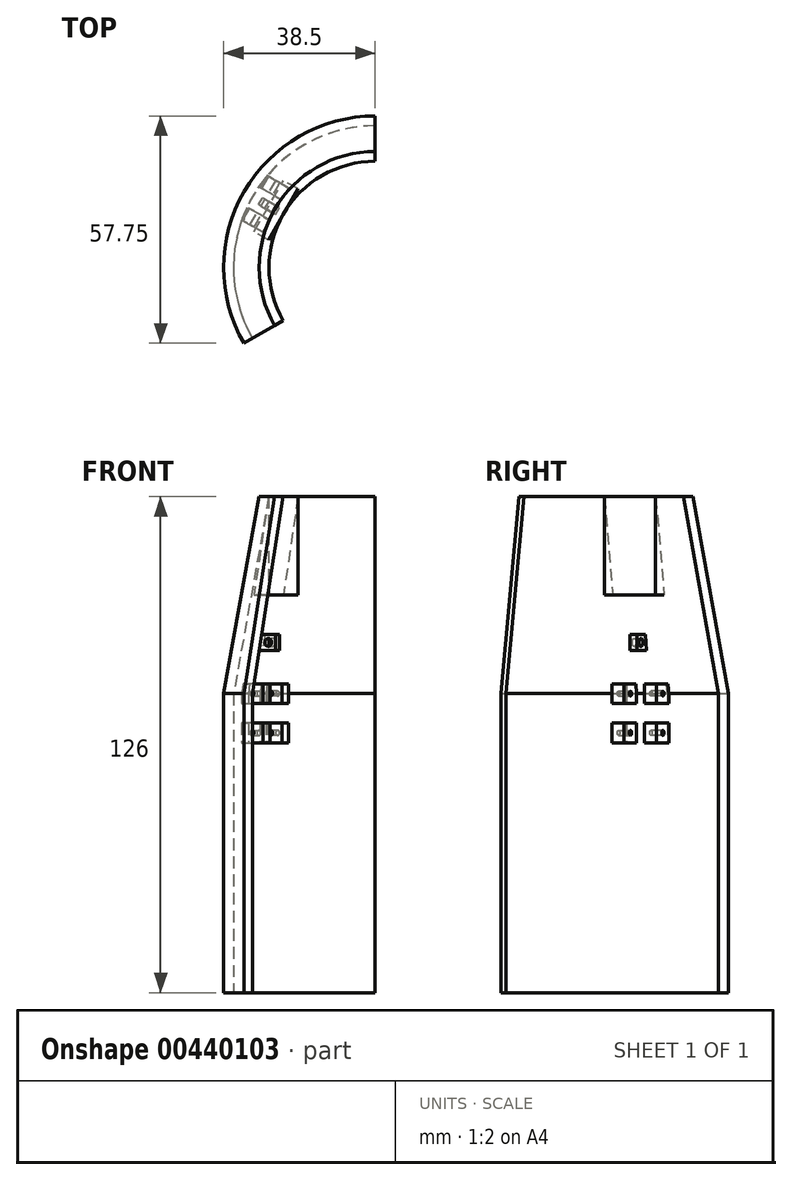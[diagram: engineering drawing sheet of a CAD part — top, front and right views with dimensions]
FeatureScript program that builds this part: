
annotation { "Feature Type Name" : "Feature", "Feature Type Description" : "" }
export const myFeature = defineFeature(function(context is Context, id is Id, definition is map)
    precondition{}
    {
        {
            var Q0;
            Q0=qCreatedBy(makeId("Top.planeOp"),FACE);
            var sketch = newSketch(context, id + "F0", { "sketchPlane" : qUnion([Q0])});
            skCircle(sketch, "E0", {"center": v(0, 0) * mm, "radius": 30 * mm});
            skCircle(sketch, "E1", {"center": v(0, 0) * mm, "radius": 27 * mm});
            skLineSegment(sketch, "E2", {"start": v(0, 0) * mm, "end": v(0, 40) * mm});
            skLineSegment(sketch, "E3", {"start": v(0, 0) * mm, "end": v(34.64, -20) * mm});
            skLineSegment(sketch, "E4", {"start": v(0, 0) * mm, "end": v(-34.64, -20) * mm});
            skCircle(sketch, "E5", {"center": v(0, 0) * mm, "radius": 19.75 * mm});
            skCircle(sketch, "E6", {"center": v(0, 0) * mm, "radius": 37 * mm});
            skCircle(sketch, "E7", {"center": v(0, 0) * mm, "radius": 40 * mm});
            skLineSegment(sketch, "E8", {"start": v(0, 0) * mm, "end": v(-34.64, 20) * mm, "construction": true});
            skLineSegment(sketch, "E9", {"start": v(-42.14, 7) * mm, "end": v(-27.14, 33) * mm, "construction": true});
            skSolve(sketch);
        }
        {
            var Q0;
            Q0=qCreatedBy(makeId("Right.planeOp"),FACE);
            var sketch = newSketch(context, id + "F1", { "sketchPlane" : qUnion([Q0])});
            skLineSegment(sketch, "E10", {"start": v(0, 0) * mm, "end": v(27, 0) * mm, "construction": true});
            skLineSegment(sketch, "E11", {"start": v(0, 0) * mm, "end": v(0, 126) * mm, "construction": true});
            skLineSegment(sketch, "E12", {"start": v(27, 0) * mm, "end": v(29.5, 0) * mm, "construction": true});
            skLineSegment(sketch, "E13", {"start": v(19.75, 0) * mm, "end": v(19.75, 126) * mm, "construction": true});
            skLineSegment(sketch, "E14", {"start": v(27, 0) * mm, "end": v(27, 126) * mm, "construction": true});
            skLineSegment(sketch, "E15", {"start": v(29.5, 0) * mm, "end": v(29.5, 126) * mm, "construction": true});
            skLineSegment(sketch, "E16", {"start": v(29.5, 0) * mm, "end": v(36, 0) * mm, "construction": true});
            skLineSegment(sketch, "E17", {"start": v(36, 0) * mm, "end": v(38.5, 0) * mm, "construction": true});
            skLineSegment(sketch, "E18", {"start": v(36, 0) * mm, "end": v(36, 126) * mm, "construction": true});
            skLineSegment(sketch, "E19", {"start": v(38.5, 0) * mm, "end": v(38.5, 126) * mm, "construction": true});
            skLineSegment(sketch, "E20", {"start": v(0, 76) * mm, "end": v(36, 76) * mm, "construction": true});
            skLineSegment(sketch, "E21", {"start": v(36, 76) * mm, "end": v(38.5, 76) * mm, "construction": true});
            skLineSegment(sketch, "E22", {"start": v(29.5, 126) * mm, "end": v(38.5, 76) * mm});
            skLineSegment(sketch, "E23", {"start": v(27, 126) * mm, "end": v(36, 76) * mm});
            skLineSegment(sketch, "E24", {"start": v(36, 76) * mm, "end": v(36, 0) * mm});
            skLineSegment(sketch, "E25", {"start": v(38.5, 76) * mm, "end": v(38.5, 0) * mm});
            skLineSegment(sketch, "E26", {"start": v(27, 126) * mm, "end": v(29.5, 126) * mm});
            skLineSegment(sketch, "E27", {"start": v(36, 0) * mm, "end": v(38.5, 0) * mm});
            skSolve(sketch);
        }
        {
            var Q0;
            Q0 = qSketchRegion(id + "F1", true);
            var Q1;
            Q1=sQuery(id+"F1.wireOp",EDGE,"E11");
            revolve(context, id + "F2", {"entities" : qUnion([Q0]), "axis" : qUnion([Q1]), "revolveType" : RevolveType.ONE_DIRECTION, "angle" : 120 * degree});
        }
        {
            var Q0;
            Q0=sQuery(id+"F0.wireOp",EDGE,"E8");
            cPlane(context, id + "F3", {"entities" : qUnion([Q0]), "cplaneType" : CPlaneType.LINE_ANGLE, "offset" : 25 * mm, "angle" : 0 * degree, "width" : 150 * mm, "height" : 150 * mm});
        }
        {
            var Q0;
            Q0=qCreatedBy(id+"F3.planeOp",FACE);
            var sketch = newSketch(context, id + "F4", { "sketchPlane" : qUnion([Q0])});
            skLineSegment(sketch, "E28", {"start": v(0, 0) * mm, "end": v(27, 0) * mm, "construction": true});
            skLineSegment(sketch, "E29", {"start": v(0, 0) * mm, "end": v(0, 126) * mm, "construction": true});
            skLineSegment(sketch, "E30", {"start": v(27, 0) * mm, "end": v(30, 0) * mm, "construction": true});
            skLineSegment(sketch, "E31", {"start": v(19.75, 0) * mm, "end": v(19.75, 126) * mm, "construction": true});
            skLineSegment(sketch, "E32", {"start": v(27, 0) * mm, "end": v(27, 126) * mm, "construction": true});
            skLineSegment(sketch, "E33", {"start": v(30, 0) * mm, "end": v(30, 126) * mm, "construction": true});
            skLineSegment(sketch, "E34", {"start": v(30, 0) * mm, "end": v(35.5, 0) * mm, "construction": true});
            skLineSegment(sketch, "E35", {"start": v(35.5, 0) * mm, "end": v(38.5, 0) * mm, "construction": true});
            skLineSegment(sketch, "E36", {"start": v(35.5, 0) * mm, "end": v(35.5, 76) * mm, "construction": true});
            skLineSegment(sketch, "E37", {"start": v(38.5, 0) * mm, "end": v(38.5, 76) * mm, "construction": true});
            skLineSegment(sketch, "E38", {"start": v(0, 76) * mm, "end": v(35.5, 76) * mm, "construction": true});
            skLineSegment(sketch, "E39", {"start": v(35.5, 76) * mm, "end": v(38.5, 76) * mm, "construction": true});
            skLineSegment(sketch, "E40", {"start": v(30, 126) * mm, "end": v(38.5, 76) * mm});
            skLineSegment(sketch, "E41", {"start": v(27, 126) * mm, "end": v(35.5, 76) * mm});
            skLineSegment(sketch, "E42", {"start": v(35.5, 76) * mm, "end": v(35.5, 0) * mm});
            skLineSegment(sketch, "E43", {"start": v(38.5, 76) * mm, "end": v(38.5, 0) * mm});
            skLineSegment(sketch, "E44", {"start": v(27, 126) * mm, "end": v(30, 126) * mm});
            skLineSegment(sketch, "E45", {"start": v(35.5, 0) * mm, "end": v(38.5, 0) * mm});
            skLineSegment(sketch, "E46.MirrorCS", {"start": v(-35.5, 0) * mm, "end": v(-38.5, 0) * mm});
            skLineSegment(sketch, "E47.MirrorCS", {"start": v(-35.5, 0) * mm, "end": v(-38.5, 0) * mm, "construction": true});
            skLineSegment(sketch, "E48.MirrorCS", {"start": v(-27, 0) * mm, "end": v(-30, 0) * mm, "construction": true});
            skLineSegment(sketch, "E49.MirrorCS", {"start": v(-27, 126) * mm, "end": v(-30, 126) * mm});
            skLineSegment(sketch, "E50.MirrorCS", {"start": v(-30, 0) * mm, "end": v(-35.5, 0) * mm, "construction": true});
            skLineSegment(sketch, "E51.MirrorCS", {"start": v(-38.5, 76) * mm, "end": v(-38.5, 0) * mm});
            skLineSegment(sketch, "E52.MirrorCS", {"start": v(-30, 0) * mm, "end": v(-30, 126) * mm, "construction": true});
            skLineSegment(sketch, "E53.MirrorCS", {"start": v(0, 0) * mm, "end": v(-27, 0) * mm, "construction": true});
            skLineSegment(sketch, "E54.MirrorCS", {"start": v(-35.5, 76) * mm, "end": v(-35.5, 0) * mm});
            skLineSegment(sketch, "E55.MirrorCS", {"start": v(-27, 0) * mm, "end": v(-27, 126) * mm, "construction": true});
            skLineSegment(sketch, "E56.MirrorCS", {"start": v(-27, 126) * mm, "end": v(-35.5, 76) * mm});
            skLineSegment(sketch, "E57.MirrorCS", {"start": v(-19.75, 0) * mm, "end": v(-19.75, 126) * mm, "construction": true});
            skLineSegment(sketch, "E58.MirrorCS", {"start": v(-35.5, 0) * mm, "end": v(-35.5, 76) * mm, "construction": true});
            skLineSegment(sketch, "E59.MirrorCS", {"start": v(-38.5, 0) * mm, "end": v(-38.5, 76) * mm, "construction": true});
            skLineSegment(sketch, "E60.MirrorCS", {"start": v(0, 76) * mm, "end": v(-35.5, 76) * mm, "construction": true});
            skLineSegment(sketch, "E61.MirrorCS", {"start": v(-30, 126) * mm, "end": v(-38.5, 76) * mm});
            skLineSegment(sketch, "E62", {"start": v(-27, 126) * mm, "end": v(-27, 101) * mm});
            skPoint(sketch, "E62.endSnap0", {"position": v(-31.25, 101) * mm});
            skLineSegment(sketch, "E63", {"start": v(-27, 101) * mm, "end": v(-31.25, 101) * mm});
            skLineSegment(sketch, "E64.left", {"start": v(-35.5, 61.36) * mm, "end": v(-35.5, 36.61) * mm});
            skLineSegment(sketch, "E64.right", {"start": v(-30, 61.36) * mm, "end": v(-30, 36.61) * mm});
            skLineSegment(sketch, "E65.left", {"start": v(-35.5, 36.61) * mm, "end": v(-35.5, 12.61) * mm});
            skLineSegment(sketch, "E65.right", {"start": v(-30, 36.61) * mm, "end": v(-30, 12.61) * mm});
            skLineSegment(sketch, "E66", {"start": v(-35.5, 73.5) * mm, "end": v(-29.14, 73.5) * mm});
            skLineSegment(sketch, "E67", {"start": v(-29.14, 73.5) * mm, "end": v(-29.14, 78.5) * mm});
            skLineSegment(sketch, "E68", {"start": v(-29.14, 78.5) * mm, "end": v(-35.08, 78.5) * mm});
            skCircle(sketch, "E69", {"center": v(-32.4, 76) * mm, "radius": 0.6 * mm});
            skPoint(sketch, "E69.centerSnap0", {"position": v(-32.1, 78.5) * mm});
            skLineSegment(sketch, "E70", {"start": v(-35.5, 63.5) * mm, "end": v(-29.13, 63.5) * mm});
            skLineSegment(sketch, "E71", {"start": v(-29.13, 63.5) * mm, "end": v(-29.13, 68.5) * mm});
            skLineSegment(sketch, "E72", {"start": v(-29.13, 68.5) * mm, "end": v(-35.5, 68.5) * mm});
            skCircle(sketch, "E73", {"center": v(-32.4, 66) * mm, "radius": 0.6 * mm});
            skPoint(sketch, "E74", {"position": v(-29.13, 66) * mm});
            skLineSegment(sketch, "E75", {"start": v(-32.95, 91) * mm, "end": v(-28.67, 91) * mm});
            skLineSegment(sketch, "E76", {"start": v(-28.67, 91) * mm, "end": v(-28.67, 87) * mm});
            skLineSegment(sketch, "E77", {"start": v(-28.67, 87) * mm, "end": v(-33.63, 87) * mm});
            skCircle(sketch, "E78", {"center": v(-30.81, 89) * mm, "radius": 1 * mm});
            skPoint(sketch, "E78.centerSnap0", {"position": v(-28.67, 89) * mm});
            skPoint(sketch, "E78.centerSnap1", {"position": v(-30.81, 91) * mm});
            skSolve(sketch);
        }
        {
            var Q0;
            {var subQ0=sQuery(id+"F4.wireOp",EDGE,"E62");Q0=makeQuery(id+"F4.imprint","IMPRINT",FACE,{"disambiguationData":[TD([[makeQuery(id+"F4.imprint","IMPRINT",EDGE,{"derivedFrom":subQ0}),-1.0]])]});}
            var Q1;
            Q1=sQuery(id+"F4.wireOp",EDGE,"E62");
            var Q2;
            Q2=sQuery(id+"F4.wireOp",EDGE,"E63");
            extrude(context, id + "F5", {"entities" : qUnion([Q0]), "surfaceEntities" : qUnion([Q1, Q2]), "endBound" : BoundingType.SYMMETRIC, "depth" : 15 * mm, "offsetDistance" : 25 * mm});
        }
        {
            var Q0;
            Q0=makeQuery(id+"F5.opExtrude","SWEPT_BODY",BODY,{"disambiguationData":[OSD([sQuery(id+"F4.wireOp",EDGE,"E56.MirrorCS"),sQuery(id+"F4.wireOp",EDGE,"E62"),sQuery(id+"F4.wireOp",EDGE,"E63")])]});
            deleteBodies(context, id + "F6", {"entities" : qUnion([Q0])});
        }
        {
            var Q0;
            {var subQ0=sQuery(id+"F4.wireOp",EDGE,"E62");Q0=makeQuery(id+"F4.imprint","IMPRINT",FACE,{"disambiguationData":[TD([[makeQuery(id+"F4.imprint","IMPRINT",EDGE,{"derivedFrom":subQ0}),-1.0]])]});}
            extrude(context, id + "F7", {"entities" : qUnion([Q0]), "endBound" : BoundingType.SYMMETRIC, "depth" : 15 * mm, "offsetDistance" : 25 * mm});
        }
        {
            var Q0;
            Q0=qCreatedBy(id+"F3.planeOp",FACE);
            cPlane(context, id + "F8", {"entities" : qUnion([Q0]), "cplaneType" : CPlaneType.OFFSET, "offset" : 3 * mm, "width" : 150 * mm, "height" : 150 * mm});
        }
        {
            var Q0;
            Q0=qCreatedBy(id+"F3.planeOp",FACE);
            cPlane(context, id + "F9", {"entities" : qUnion([Q0]), "cplaneType" : CPlaneType.OFFSET, "offset" : 3 * mm, "oppositeDirection" : true, "width" : 150 * mm, "height" : 150 * mm});
        }
        {
            var Q0;
            Q0=qCreatedBy(id+"F8.planeOp",FACE);
            var sketch = newSketch(context, id + "F10", { "sketchPlane" : qUnion([Q0])});
            skLineSegment(sketch, "E79", {"start": v(0, 0) * mm, "end": v(0, 76) * mm});
            skLineSegment(sketch, "E80.0.0", {"start": v(-29.14, 73.5) * mm, "end": v(-29.14, 78.5) * mm});
            skLineSegment(sketch, "E80.0.1", {"start": v(-29.14, 78.5) * mm, "end": v(-35.08, 78.5) * mm});
            skLineSegment(sketch, "E80.0.2", {"start": v(-35.08, 78.5) * mm, "end": v(-35.5, 76) * mm});
            skLineSegment(sketch, "E80.0.3", {"start": v(-35.5, 76) * mm, "end": v(-35.5, 73.5) * mm});
            skLineSegment(sketch, "E80.0.4", {"start": v(-35.5, 73.5) * mm, "end": v(-29.14, 73.5) * mm});
            skLineSegment(sketch, "E80.1.0", {"start": v(-29.13, 63.5) * mm, "end": v(-29.13, 68.5) * mm});
            skLineSegment(sketch, "E80.1.1", {"start": v(-29.13, 68.5) * mm, "end": v(-35.5, 68.5) * mm});
            skLineSegment(sketch, "E80.1.2", {"start": v(-35.5, 68.5) * mm, "end": v(-35.5, 63.5) * mm});
            skLineSegment(sketch, "E80.1.3", {"start": v(-35.5, 63.5) * mm, "end": v(-29.13, 63.5) * mm});
            skCircle(sketch, "E80.2", {"center": v(-32.4, 66) * mm, "radius": 0.6 * mm});
            skCircle(sketch, "E80.3", {"center": v(-32.4, 76) * mm, "radius": 0.6 * mm});
            skSolve(sketch);
        }
        {
            var Q0;
            Q0=qCreatedBy(id+"F9.planeOp",FACE);
            var sketch = newSketch(context, id + "F11", { "sketchPlane" : qUnion([Q0])});
            skLineSegment(sketch, "E81.0.0", {"start": v(-29.14, 73.5) * mm, "end": v(-29.14, 78.5) * mm});
            skLineSegment(sketch, "E81.0.1", {"start": v(-29.14, 78.5) * mm, "end": v(-35.08, 78.5) * mm});
            skLineSegment(sketch, "E81.0.2", {"start": v(-35.08, 78.5) * mm, "end": v(-35.5, 76) * mm});
            skLineSegment(sketch, "E81.0.3", {"start": v(-35.5, 76) * mm, "end": v(-35.5, 73.5) * mm});
            skLineSegment(sketch, "E81.0.4", {"start": v(-35.5, 73.5) * mm, "end": v(-29.14, 73.5) * mm});
            skLineSegment(sketch, "E81.1.0", {"start": v(-29.13, 63.5) * mm, "end": v(-29.13, 68.5) * mm});
            skLineSegment(sketch, "E81.1.1", {"start": v(-29.13, 68.5) * mm, "end": v(-35.5, 68.5) * mm});
            skLineSegment(sketch, "E81.1.2", {"start": v(-35.5, 68.5) * mm, "end": v(-35.5, 63.5) * mm});
            skLineSegment(sketch, "E81.1.3", {"start": v(-35.5, 63.5) * mm, "end": v(-29.13, 63.5) * mm});
            skCircle(sketch, "E81.2", {"center": v(-32.4, 66) * mm, "radius": 0.6 * mm});
            skCircle(sketch, "E81.3", {"center": v(-32.4, 76) * mm, "radius": 0.6 * mm});
            skSolve(sketch);
        }
        {
            var Q0;
            Q0=makeQuery(id+"F11.imprint","IMPRINT",FACE,{"disambiguationData":[TD([[makeQuery(id+"F11.imprint","IMPRINT",EDGE,{"derivedFrom":sQuery(id+"F11.wireOp",EDGE,"E81.0.0")}),1.0]])]});
            var Q1;
            Q1=makeQuery(id+"F11.imprint","IMPRINT",FACE,{"disambiguationData":[TD([[makeQuery(id+"F11.imprint","IMPRINT",EDGE,{"derivedFrom":sQuery(id+"F11.wireOp",EDGE,"E81.1.0")}),1.0]])]});
            extrude(context, id + "F12", {"entities" : qUnion([Q0, Q1]), "operationType" : NewBodyOperationType.ADD, "oppositeDirection" : true, "depth" : 3.5 * mm, "offsetDistance" : 25 * mm});
        }
        {
            var Q0;
            Q0=makeQuery(id+"F10.imprint","IMPRINT",FACE,{"disambiguationData":[TD([[makeQuery(id+"F10.imprint","IMPRINT",EDGE,{"derivedFrom":sQuery(id+"F10.wireOp",EDGE,"E80.0.0")}),1.0]])]});
            var Q1;
            Q1=makeQuery(id+"F10.imprint","IMPRINT",FACE,{"disambiguationData":[TD([[makeQuery(id+"F10.imprint","IMPRINT",EDGE,{"derivedFrom":sQuery(id+"F10.wireOp",EDGE,"E80.1.0")}),1.0]])]});
            extrude(context, id + "F13", {"entities" : qUnion([Q0, Q1]), "operationType" : NewBodyOperationType.ADD, "depth" : 3.5 * mm, "offsetDistance" : 25 * mm});
        }
        {
            var Q0;
            {var subQ1=sQuery(id+"F4.wireOp",EDGE,"E75");Q0=makeQuery(id+"F4.imprint","IMPRINT",FACE,{"disambiguationData":[TD([[makeQuery(id+"F4.imprint","IMPRINT",EDGE,{"derivedFrom":subQ1}),-1.0]])]});}
            extrude(context, id + "F14", {"entities" : qUnion([Q0]), "operationType" : NewBodyOperationType.ADD, "endBound" : BoundingType.SYMMETRIC, "depth" : 2 * mm, "offsetDistance" : 25 * mm});
        }
    });
